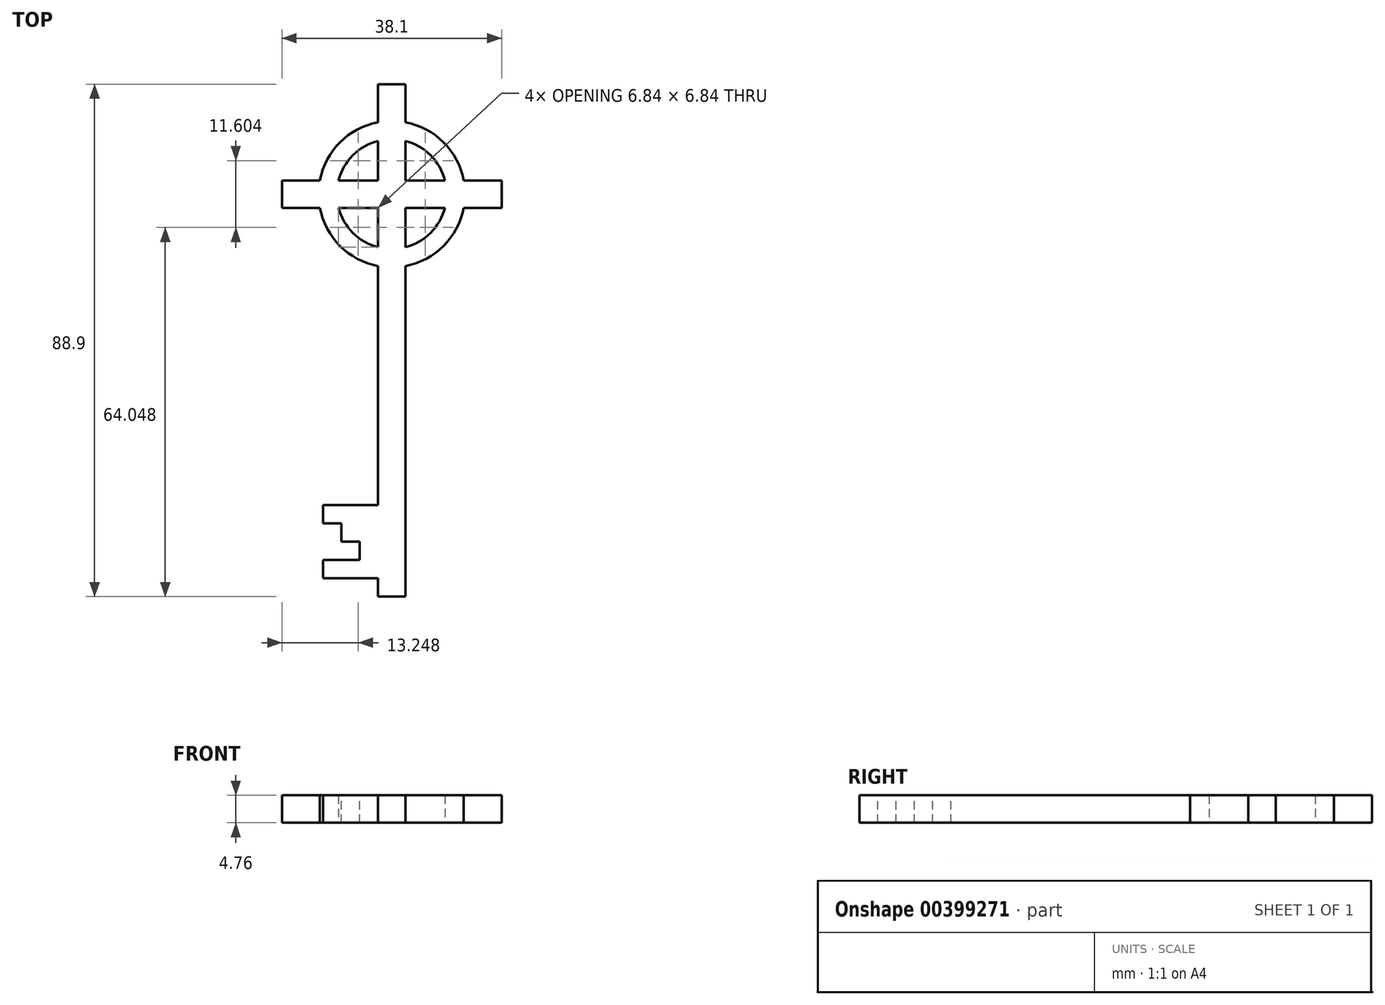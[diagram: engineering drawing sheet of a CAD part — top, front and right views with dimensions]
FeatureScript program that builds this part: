
annotation { "Feature Type Name" : "Feature", "Feature Type Description" : "" }
export const myFeature = defineFeature(function(context is Context, id is Id, definition is map)
    precondition{}
    {
        {
            var Q0;
            Q0=qCreatedBy(makeId("Top.planeOp"),FACE);
            var sketch = newSketch(context, id + "F0", { "sketchPlane" : qUnion([Q0])});
            skCircle(sketch, "E0", {"center": v(0, 0) * mm, "radius": 12.7 * mm});
            skCircle(sketch, "E1", {"center": v(0, 0) * mm, "radius": 9.53 * mm});
            skSolve(sketch);
        }
        {
            var Q0;
            Q0 = qSketchRegion(id + "F0", true);
            extrude(context, id + "F1", {"entities" : qUnion([Q0]), "depth" : 4.76 * mm});
        }
        {
            var Q0;
            Q0=makeQuery(id+"F1.opExtrude","CAP_FACE",FACE,{"disambiguationData":[OSD([sQuery(id+"F0.wireOp",EDGE,"E0"),sQuery(id+"F0.wireOp",EDGE,"E1")])],"isStart":false});
            var sketch = newSketch(context, id + "F2", { "sketchPlane" : qUnion([Q0])});
            skLineSegment(sketch, "E2.bottom", {"start": v(19.05, 2.38) * mm, "end": v(-19.05, 2.38) * mm});
            skLineSegment(sketch, "E2.top", {"start": v(19.05, -2.38) * mm, "end": v(-19.05, -2.38) * mm});
            skLineSegment(sketch, "E2.left", {"start": v(19.05, 2.38) * mm, "end": v(19.05, -2.38) * mm});
            skLineSegment(sketch, "E2.right", {"start": v(-19.05, 2.38) * mm, "end": v(-19.05, -2.38) * mm});
            skPoint(sketch, "E2.middle", {"position": v(0, 0) * mm});
            skSolve(sketch);
        }
        {
            var Q0;
            Q0 = qSketchRegion(id + "F2", true);
            extrude(context, id + "F3", {"entities" : qUnion([Q0]), "operationType" : NewBodyOperationType.ADD, "oppositeDirection" : true, "depth" : 4.76 * mm});
        }
        {
            var Q0;
            Q0=makeQuery(id+"F3.boolean.opBoolean","MERGE",FACE,{"derivedFrom":[makeQuery(id+"F1.opExtrude","CAP_FACE",FACE,{"disambiguationData":[OSD([sQuery(id+"F0.wireOp",EDGE,"E0"),sQuery(id+"F0.wireOp",EDGE,"E1")])],"isStart":false}),makeQuery(id+"F3.opExtrude","CAP_FACE",FACE,{"disambiguationData":[OSD([sQuery(id+"F2.wireOp",EDGE,"E2.bottom"),sQuery(id+"F2.wireOp",EDGE,"E2.top"),sQuery(id+"F2.wireOp",EDGE,"E2.left"),sQuery(id+"F2.wireOp",EDGE,"E2.right")])],"isStart":true})]});
            var sketch = newSketch(context, id + "F4", { "sketchPlane" : qUnion([Q0])});
            skLineSegment(sketch, "E3.bottom", {"start": v(-2.38, 19.05) * mm, "end": v(2.38, 19.05) * mm});
            skLineSegment(sketch, "E3.top", {"start": v(-2.38, -69.85) * mm, "end": v(2.38, -69.85) * mm});
            skLineSegment(sketch, "E3.left", {"start": v(-2.38, 19.05) * mm, "end": v(-2.38, -69.85) * mm});
            skLineSegment(sketch, "E3.right", {"start": v(2.38, 19.05) * mm, "end": v(2.38, -69.85) * mm});
            skPoint(sketch, "E3.middle", {"position": v(0, -25.4) * mm});
            skSolve(sketch);
        }
        {
            var Q0;
            Q0 = qSketchRegion(id + "F4", true);
            extrude(context, id + "F5", {"entities" : qUnion([Q0]), "operationType" : NewBodyOperationType.ADD, "oppositeDirection" : true, "depth" : 4.76 * mm});
        }
        {
            var Q0;
            Q0=makeQuery(id+"F5.boolean.opBoolean","MERGE",FACE,{"derivedFrom":[makeQuery(id+"F3.boolean.opBoolean","MERGE",FACE,{"derivedFrom":[makeQuery(id+"F1.opExtrude","CAP_FACE",FACE,{"disambiguationData":[OSD([sQuery(id+"F0.wireOp",EDGE,"E0"),sQuery(id+"F0.wireOp",EDGE,"E1")])],"isStart":false}),makeQuery(id+"F3.opExtrude","CAP_FACE",FACE,{"disambiguationData":[OSD([sQuery(id+"F2.wireOp",EDGE,"E2.bottom"),sQuery(id+"F2.wireOp",EDGE,"E2.top"),sQuery(id+"F2.wireOp",EDGE,"E2.left"),sQuery(id+"F2.wireOp",EDGE,"E2.right")])],"isStart":true})]}),makeQuery(id+"F5.opExtrude","CAP_FACE",FACE,{"disambiguationData":[OSD([sQuery(id+"F4.wireOp",EDGE,"E3.bottom"),sQuery(id+"F4.wireOp",EDGE,"E3.top"),sQuery(id+"F4.wireOp",EDGE,"E3.left"),sQuery(id+"F4.wireOp",EDGE,"E3.right")])],"isStart":true})]});
            var sketch = newSketch(context, id + "F6", { "sketchPlane" : qUnion([Q0])});
            skLineSegment(sketch, "E4", {"start": v(-2.38, -53.98) * mm, "end": v(-11.9, -53.98) * mm});
            skLineSegment(sketch, "E5", {"start": v(-11.9, -53.98) * mm, "end": v(-11.9, -57.15) * mm});
            skLineSegment(sketch, "E6", {"start": v(-11.9, -57.15) * mm, "end": v(-8.73, -57.15) * mm});
            skLineSegment(sketch, "E7", {"start": v(-8.73, -57.15) * mm, "end": v(-8.73, -60.33) * mm});
            skLineSegment(sketch, "E8", {"start": v(-8.73, -60.33) * mm, "end": v(-5.56, -60.33) * mm});
            skLineSegment(sketch, "E9", {"start": v(-5.56, -60.33) * mm, "end": v(-5.56, -63.5) * mm});
            skLineSegment(sketch, "E10", {"start": v(-5.56, -63.5) * mm, "end": v(-11.9, -63.5) * mm});
            skLineSegment(sketch, "E11", {"start": v(-11.9, -63.5) * mm, "end": v(-11.9, -66.68) * mm});
            skLineSegment(sketch, "E12", {"start": v(-11.9, -66.68) * mm, "end": v(-2.38, -66.68) * mm});
            skLineSegment(sketch, "E13", {"start": v(-2.38, -66.68) * mm, "end": v(-2.38, -53.98) * mm});
            skSolve(sketch);
        }
        {
            var Q0;
            Q0 = qSketchRegion(id + "F6", true);
            extrude(context, id + "F7", {"entities" : qUnion([Q0]), "operationType" : NewBodyOperationType.ADD, "oppositeDirection" : true, "depth" : 4.76 * mm});
        }
    });
